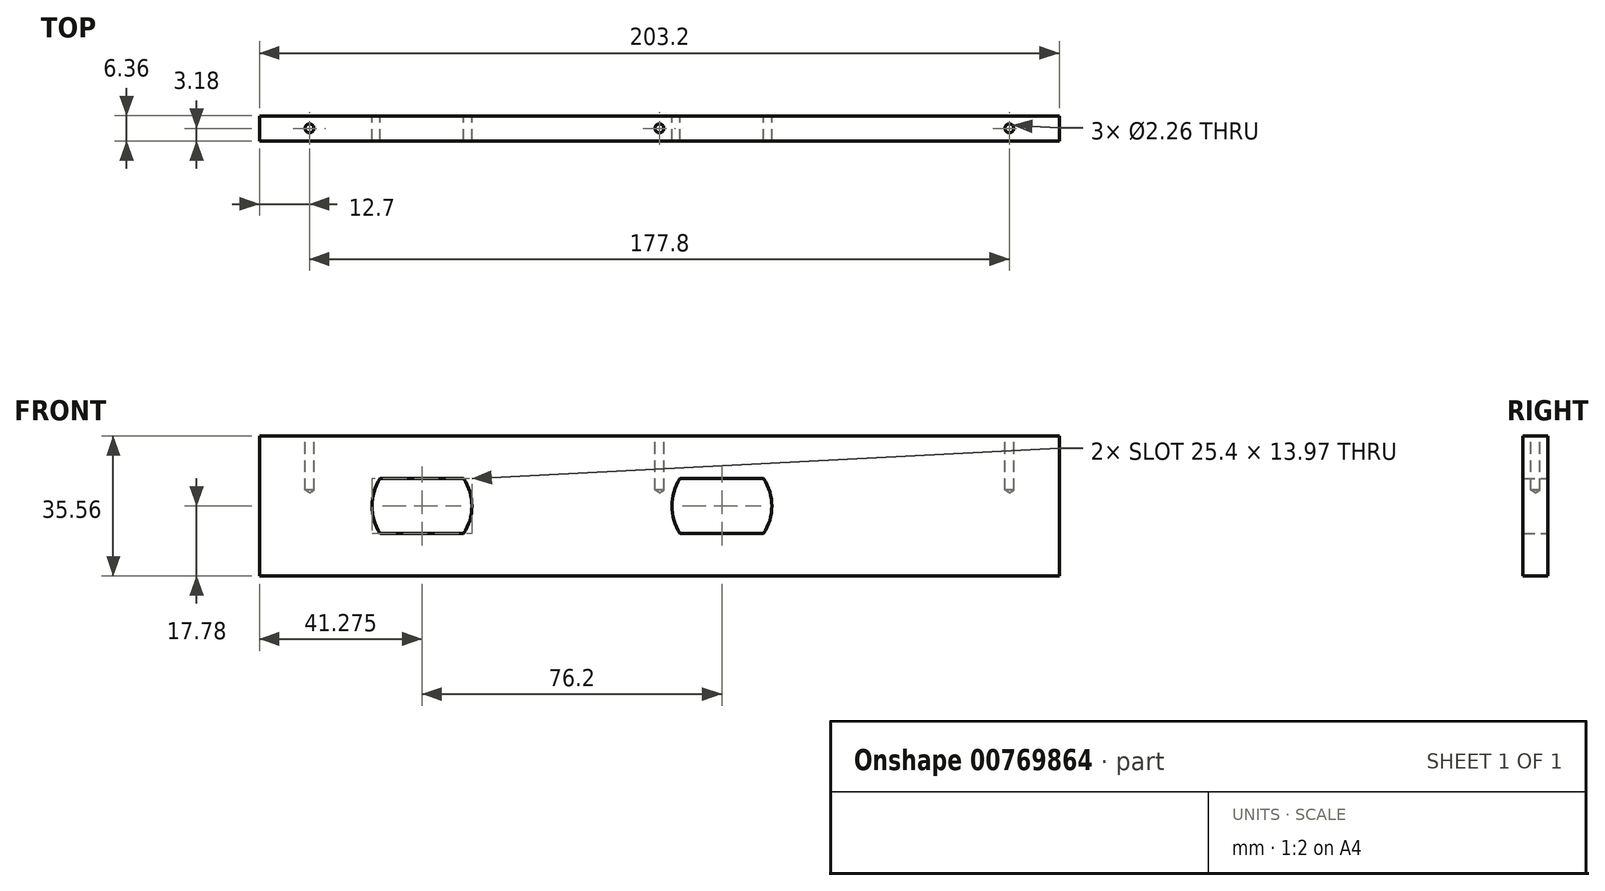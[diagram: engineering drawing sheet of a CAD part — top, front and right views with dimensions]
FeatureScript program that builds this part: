
annotation { "Feature Type Name" : "Feature", "Feature Type Description" : "" }
export const myFeature = defineFeature(function(context is Context, id is Id, definition is map)
    precondition{}
    {
        {
            var Q0;
            Q0=qCreatedBy(makeId("Top.planeOp"),FACE);
            var sketch = newSketch(context, id + "F0", { "sketchPlane" : qUnion([Q0])});
            skLineSegment(sketch, "E0.bottom", {"start": v(-101.6, 3.18) * mm, "end": v(101.6, 3.18) * mm});
            skLineSegment(sketch, "E0.top", {"start": v(-101.6, -3.18) * mm, "end": v(101.6, -3.18) * mm});
            skLineSegment(sketch, "E0.left", {"start": v(-101.6, 3.18) * mm, "end": v(-101.6, -3.17) * mm});
            skLineSegment(sketch, "E0.right", {"start": v(101.6, 3.18) * mm, "end": v(101.6, -3.17) * mm});
            skLineSegment(sketch, "E1", {"start": v(-101.6, 3.18) * mm, "end": v(101.6, -3.17) * mm, "construction": true});
            skSolve(sketch);
        }
        {
            var Q0;
            Q0=qSketchRegion(id+"F0",true);
            extrude(context, id + "F1", {"entities" : qUnion([Q0]), "depth" : 35.56 * mm, "offsetDistance" : 25.4 * mm});
        }
        {
            var Q0;
            Q0=makeQuery(id+"F1.opExtrude","CAP_FACE",FACE,{"disambiguationData":[OSD([sQuery(id+"F0.wireOp",EDGE,"E0.bottom"),sQuery(id+"F0.wireOp",EDGE,"E0.top"),sQuery(id+"F0.wireOp",EDGE,"E0.left"),sQuery(id+"F0.wireOp",EDGE,"E0.right")])],"isStart":false});
            var sketch = newSketch(context, id + "F2", { "sketchPlane" : qUnion([Q0])});
            skLineSegment(sketch, "E2", {"start": v(-101.6, 0) * mm, "end": v(101.6, 0) * mm, "construction": true});
            skPoint(sketch, "E3", {"position": v(-88.9, 0) * mm});
            skPoint(sketch, "E4", {"position": v(88.9, 0) * mm});
            skPoint(sketch, "E5", {"position": v(0, 0) * mm});
            skSolve(sketch);
        }
        {
            var Q0;
            Q0=sQuery(id+"F2.wireOp",VERTEX,"E5");
            var Q1;
            Q1=sQuery(id+"F2.wireOp",VERTEX,"E4");
            var Q2;
            Q2=sQuery(id+"F2.wireOp",VERTEX,"E3");
            var Q3;
            Q3=makeQuery(id+"F1.opExtrude","SWEPT_BODY",BODY,{"disambiguationData":[OSD([sQuery(id+"F0.wireOp",EDGE,"E0.bottom"),sQuery(id+"F0.wireOp",EDGE,"E0.top"),sQuery(id+"F0.wireOp",EDGE,"E0.left"),sQuery(id+"F0.wireOp",EDGE,"E0.right")])]});
            hole(context, id + "F3", {"style" : HoleStyle.SIMPLE, "endStyle" : HoleEndStyle.BLIND, "standardTappedOrClearance" : lookupTablePath({ "standard" : "ANSI", "engagement" : "75%", "pitch" : "40 tpi", "size" : "#4", "type" : "Tapped" }), "standardBlindInLast" : lookupTablePath({ "standard" : "ANSI", "engagement" : "75%", "pitch" : "40 tpi", "size" : "#4", "type" : "Tapped" }), "holeDiameter" : 2.26 * mm, "majorDiameter" : 2.84 * mm, "showTappedDepth" : true, "holeDepth" : 13.75 * mm, "tappedDepth" : 11.84 * mm, "tapClearance" : 3, "locations" : qUnion([Q0, Q1, Q2]), "scope" : qUnion([Q3])});
        }
        {
            var Q0;
            Q0=makeQuery(id+"F1.opExtrude","SWEPT_FACE",FACE,{"disambiguationData":[OSD([sQuery(id+"F0.wireOp",EDGE,"E0.bottom")])]});
            var sketch = newSketch(context, id + "F4", { "sketchPlane" : qUnion([Q0])});
            skLineSegment(sketch, "E6", {"start": v(-101.6, 17.78) * mm, "end": v(101.6, 17.78) * mm, "construction": true});
            skPoint(sketch, "E7", {"position": v(-15.87, 17.78) * mm});
            skPoint(sketch, "E8", {"position": v(60.33, 17.78) * mm});
            skArc(sketch, "E9", {"start": v(49.72, 24.77) * mm, "mid": v(47.63, 17.78) * mm, "end": v(49.72, 10.8) * mm});
            skArc(sketch, "E10", {"start": v(-5.27, 10.8) * mm, "mid": v(-3.17, 17.78) * mm, "end": v(-5.27, 24.77) * mm});
            skLineSegment(sketch, "E11", {"start": v(70.93, 24.77) * mm, "end": v(49.72, 24.77) * mm});
            skLineSegment(sketch, "E12", {"start": v(49.72, 24.77) * mm, "end": v(-5.27, 24.77) * mm, "construction": true});
            skLineSegment(sketch, "E13", {"start": v(-5.27, 24.77) * mm, "end": v(-26.48, 24.77) * mm});
            skLineSegment(sketch, "E14", {"start": v(70.93, 10.8) * mm, "end": v(49.72, 10.8) * mm});
            skLineSegment(sketch, "E15", {"start": v(49.72, 10.8) * mm, "end": v(-5.27, 10.8) * mm, "construction": true});
            skLineSegment(sketch, "E16", {"start": v(-5.27, 10.8) * mm, "end": v(-26.48, 10.8) * mm});
            skArc(sketch, "E17.trimOffspring", {"start": v(70.93, 10.8) * mm, "mid": v(73.03, 17.78) * mm, "end": v(70.93, 24.77) * mm});
            skArc(sketch, "E18.trimOffspring", {"start": v(-26.48, 24.77) * mm, "mid": v(-28.57, 17.78) * mm, "end": v(-26.48, 10.8) * mm});
            skSolve(sketch);
        }
        {
            var Q0;
            Q0 = qSketchRegion(id + "F4", true);
            extrude(context, id + "F5", {"entities" : qUnion([Q0]), "operationType" : NewBodyOperationType.REMOVE, "endBound" : BoundingType.THROUGH_ALL, "oppositeDirection" : true, "depth" : 25.4 * mm, "offsetDistance" : 25.4 * mm});
        }
    });
